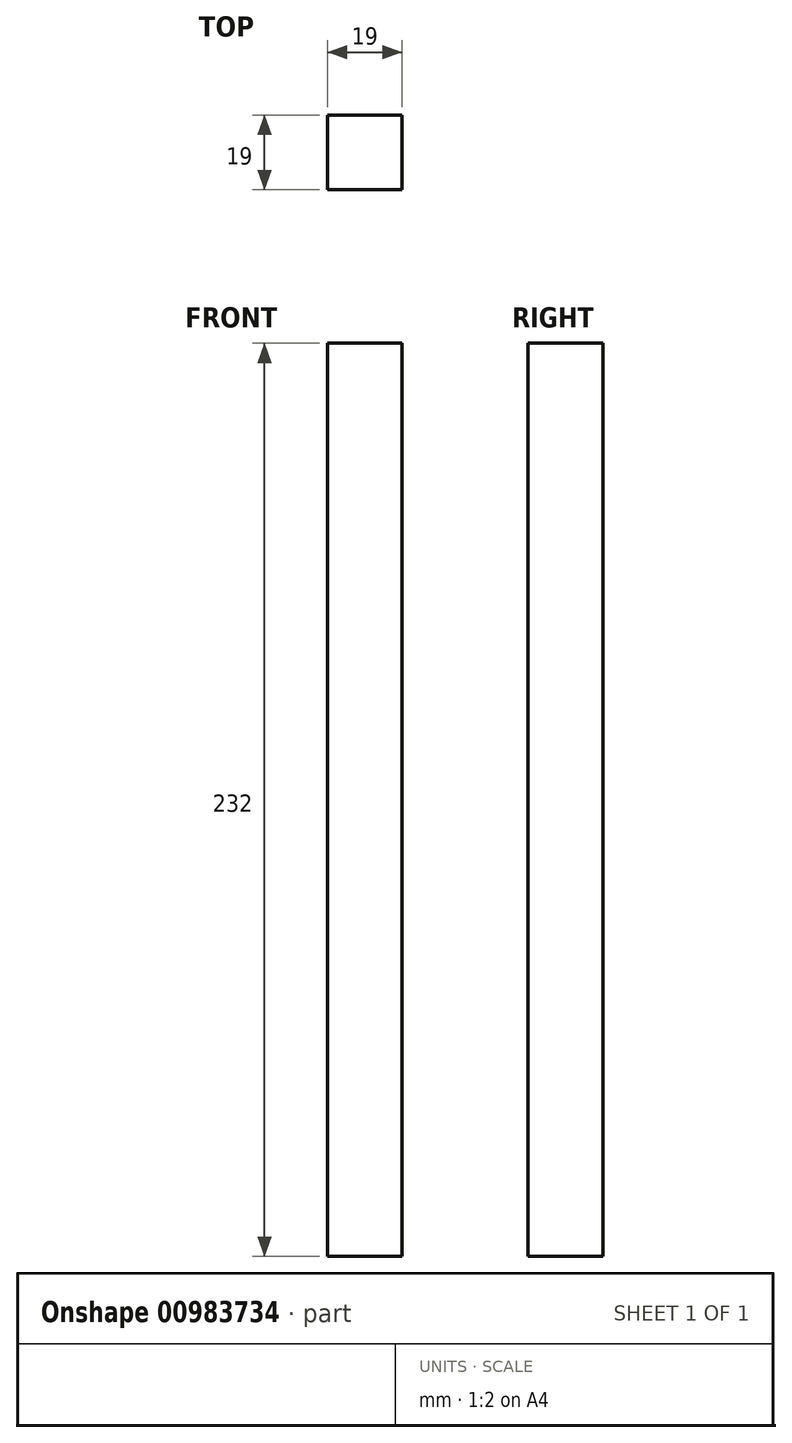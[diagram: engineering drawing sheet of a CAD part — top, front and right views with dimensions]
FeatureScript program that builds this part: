
annotation { "Feature Type Name" : "Feature", "Feature Type Description" : "" }
export const myFeature = defineFeature(function(context is Context, id is Id, definition is map)
    precondition{}
    {
        {
            var Q0;
            Q0=qCreatedBy(makeId("Front.planeOp"),FACE);
            var sketch = newSketch(context, id + "F0", { "sketchPlane" : qUnion([Q0])});
            skLineSegment(sketch, "E0.bottom", {"start": v(-45.32, 232) * mm, "end": v(-26.32, 232) * mm});
            skLineSegment(sketch, "E0.top", {"start": v(-45.32, 0) * mm, "end": v(-26.32, 0) * mm});
            skLineSegment(sketch, "E0.left", {"start": v(-45.32, 232) * mm, "end": v(-45.32, 0) * mm});
            skLineSegment(sketch, "E0.right", {"start": v(-26.32, 232) * mm, "end": v(-26.32, 0) * mm});
            skSolve(sketch);
        }
        {
            var Q0;
            Q0 = qSketchRegion(id + "F0", true);
            extrude(context, id + "F1", {"entities" : qUnion([Q0]), "depth" : 19 * mm, "offsetDistance" : 25.4 * mm});
        }
        {
            var Q0;
            Q0 = qSketchRegion(id + "F0", true);
            var Q1;
            Q1=makeQuery(id+"F1.opExtrude","CAP_FACE",FACE,{"disambiguationData":[OSD([sQuery(id+"F0.wireOp",EDGE,"E0.bottom"),sQuery(id+"F0.wireOp",EDGE,"E0.top"),sQuery(id+"F0.wireOp",EDGE,"E0.left"),sQuery(id+"F0.wireOp",EDGE,"E0.right")])],"isStart":true});
            extrude(context, id + "F2", {"entities" : qUnion([Q0, Q1]), "operationType" : NewBodyOperationType.ADD, "depth" : 19 * mm, "offsetDistance" : 25.4 * mm});
        }
    });
